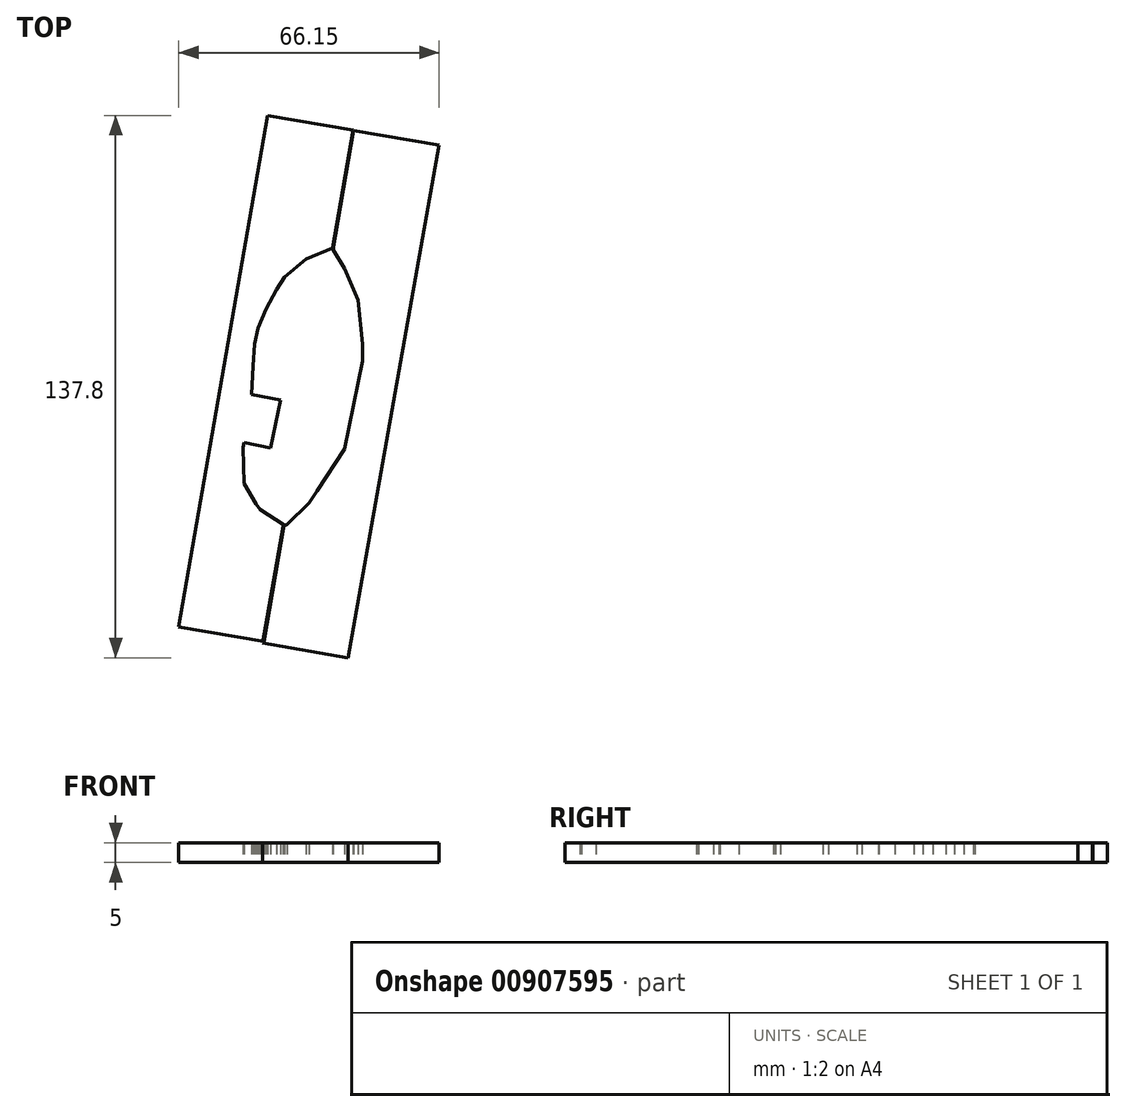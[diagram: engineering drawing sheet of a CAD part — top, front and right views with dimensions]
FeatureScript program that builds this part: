
annotation { "Feature Type Name" : "Feature", "Feature Type Description" : "" }
export const myFeature = defineFeature(function(context is Context, id is Id, definition is map)
    precondition{}
    {
        {
            var Q0;
            Q0=qCreatedBy(makeId("Top.planeOp"),FACE);
            var sketch = newSketch(context, id + "F0", { "sketchPlane" : qUnion([Q0])});
            skLineSegment(sketch, "E0", {"start": v(-30.94, 53.41) * mm, "end": v(6.08, 46.46) * mm});
            skLineSegment(sketch, "E1", {"start": v(-10.77, 49.62) * mm, "end": v(-27.45, -47.68) * mm});
            skSolve(sketch);
        }
        {
            var Q0;
            Q0=qCreatedBy(makeId("Top.planeOp"),FACE);
            var sketch = newSketch(context, id + "F1", { "sketchPlane" : qUnion([Q0])});
            skLineSegment(sketch, "E2", {"start": v(-12.64, 39.88) * mm, "end": v(-19.45, 37.13) * mm});
            skLineSegment(sketch, "E3", {"start": v(-19.45, 37.13) * mm, "end": v(-24.95, 32.5) * mm});
            skLineSegment(sketch, "E4", {"start": v(-24.95, 32.5) * mm, "end": v(-26.98, 29.31) * mm});
            skLineSegment(sketch, "E5", {"start": v(-26.98, 29.31) * mm, "end": v(-29.59, 24.39) * mm});
            skLineSegment(sketch, "E6", {"start": v(-29.59, 24.39) * mm, "end": v(-31.61, 19.6) * mm});
            skLineSegment(sketch, "E7", {"start": v(-31.61, 19.6) * mm, "end": v(-32.48, 15.46) * mm});
            skLineSegment(sketch, "E8", {"start": v(-32.48, 15.46) * mm, "end": v(-32.94, 9.98) * mm});
            skLineSegment(sketch, "E9", {"start": v(-32.94, 9.98) * mm, "end": v(-33.3, 2.73) * mm});
            skLineSegment(sketch, "E10", {"start": v(-33.3, 2.73) * mm, "end": v(-25.88, 1.29) * mm});
            skLineSegment(sketch, "E11", {"start": v(-25.88, 1.29) * mm, "end": v(-28.39, -10.91) * mm});
            skPoint(sketch, "E12.end.orphan", {"position": v(-28.39, -11.57) * mm});
            skLineSegment(sketch, "E13", {"start": v(-12.64, 39.88) * mm, "end": v(-7.5, 69.88) * mm});
            skLineSegment(sketch, "E14", {"start": v(-7.5, 69.88) * mm, "end": v(-29.18, 73.6) * mm});
            skLineSegment(sketch, "E15", {"start": v(-28.39, -10.91) * mm, "end": v(-35.13, -9.53) * mm});
            skLineSegment(sketch, "E16", {"start": v(-35.13, -9.53) * mm, "end": v(-35.39, -10.8) * mm});
            skLineSegment(sketch, "E17", {"start": v(-35.39, -10.8) * mm, "end": v(-35.13, -19.96) * mm});
            skLineSegment(sketch, "E18", {"start": v(-35.13, -19.96) * mm, "end": v(-32.08, -25.07) * mm});
            skLineSegment(sketch, "E19", {"start": v(-32.08, -25.07) * mm, "end": v(-31.07, -26.5) * mm});
            skLineSegment(sketch, "E20", {"start": v(-31.07, -26.5) * mm, "end": v(-25.02, -30.47) * mm});
            skLineSegment(sketch, "E21", {"start": v(-25.02, -30.47) * mm, "end": v(-30.1, -60.04) * mm});
            skLineSegment(sketch, "E22", {"start": v(-30.1, -60.04) * mm, "end": v(-51.78, -56.32) * mm});
            skLineSegment(sketch, "E23", {"start": v(-51.78, -56.32) * mm, "end": v(-29.18, 73.6) * mm});
            skSolve(sketch);
        }
        {
            var Q0;
            Q0 = qSketchRegion(id + "F1", true);
            extrude(context, id + "F2", {"entities" : qUnion([Q0]), "depth" : 5 * mm, "offsetDistance" : 25 * mm});
        }
        {
            var Q0;
            Q0=qCreatedBy(makeId("Top.planeOp"),FACE);
            var sketch = newSketch(context, id + "F3", { "sketchPlane" : qUnion([Q0])});
            skLineSegment(sketch, "E24", {"start": v(-12.54, 39.53) * mm, "end": v(-9.6, 34.67) * mm});
            skLineSegment(sketch, "E25", {"start": v(-9.6, 34.67) * mm, "end": v(-6.26, 26.73) * mm});
            skLineSegment(sketch, "E26", {"start": v(-6.26, 26.73) * mm, "end": v(-5.1, 15.57) * mm});
            skLineSegment(sketch, "E27", {"start": v(-5.1, 15.57) * mm, "end": v(-5.1, 11.24) * mm});
            skLineSegment(sketch, "E28", {"start": v(-5.1, 11.24) * mm, "end": v(-9.6, -11.2) * mm});
            skLineSegment(sketch, "E29", {"start": v(-9.6, -11.2) * mm, "end": v(-16.66, -21.83) * mm});
            skLineSegment(sketch, "E30", {"start": v(-16.66, -21.83) * mm, "end": v(-18.69, -24.87) * mm});
            skLineSegment(sketch, "E31", {"start": v(-18.69, -24.87) * mm, "end": v(-24.26, -30.27) * mm});
            skLineSegment(sketch, "E32", {"start": v(-12.54, 39.53) * mm, "end": v(-7.3, 69.79) * mm});
            skLineSegment(sketch, "E33", {"start": v(-24.26, -30.27) * mm, "end": v(-25.26, -30.85) * mm});
            skLineSegment(sketch, "E34", {"start": v(-25.26, -30.85) * mm, "end": v(-30.45, -60.4) * mm});
            skLineSegment(sketch, "E35", {"start": v(-30.45, -60.4) * mm, "end": v(-8.78, -64.2) * mm});
            skLineSegment(sketch, "E36", {"start": v(-7.3, 69.79) * mm, "end": v(14.37, 66.04) * mm});
            skLineSegment(sketch, "E37", {"start": v(-8.78, -64.2) * mm, "end": v(14.37, 66.04) * mm});
            skSolve(sketch);
        }
        {
            var Q0;
            Q0 = qSketchRegion(id + "F3", true);
            extrude(context, id + "F4", {"entities" : qUnion([Q0]), "depth" : 5 * mm, "offsetDistance" : 25 * mm});
        }
    });
